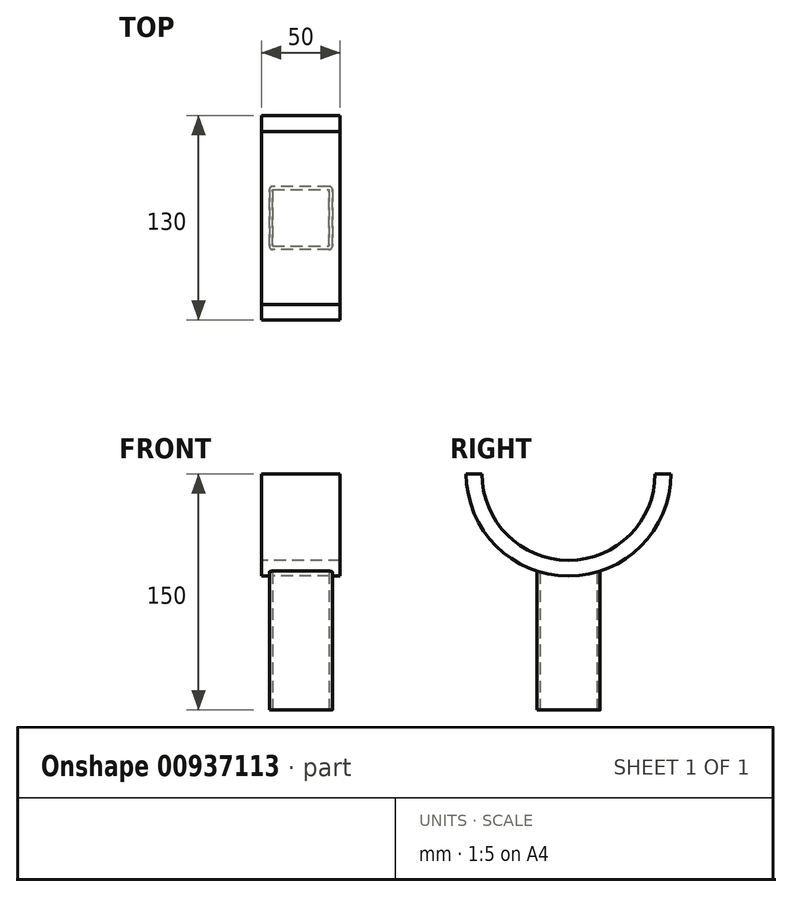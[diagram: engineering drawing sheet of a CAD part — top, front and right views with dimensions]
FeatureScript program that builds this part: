
annotation { "Feature Type Name" : "Feature", "Feature Type Description" : "" }
export const myFeature = defineFeature(function(context is Context, id is Id, definition is map)
    precondition{}
    {
        {
            var Q0;
            Q0=qCreatedBy(makeId("Right.planeOp"),FACE);
            var sketch = newSketch(context, id + "F0", { "sketchPlane" : qUnion([Q0])});
            skArc(sketch, "E0", {"start": v(55, 0) * mm, "mid": v(0, -55) * mm, "end": v(-55, 0) * mm});
            skArc(sketch, "E1.0", {"start": v(65, 0) * mm, "mid": v(0, -65) * mm, "end": v(-65, 0) * mm});
            skLineSegment(sketch, "E2", {"start": v(-65, 0) * mm, "end": v(-55, 0) * mm});
            skLineSegment(sketch, "E3", {"start": v(55, 0) * mm, "end": v(65, 0) * mm});
            skSolve(sketch);
        }
        {
            var Q0;
            Q0 = qSketchRegion(id + "F0", true);
            extrude(context, id + "F1", {"entities" : qUnion([Q0]), "endBound" : BoundingType.SYMMETRIC, "depth" : 50 * mm, "offsetDistance" : 25 * mm});
        }
        {
            var Q0;
            Q0=qCreatedBy(makeId("Top.planeOp"),FACE);
            cPlane(context, id + "F2", {"entities" : qUnion([Q0]), "cplaneType" : CPlaneType.OFFSET, "offset" : 150 * mm, "oppositeDirection" : true, "width" : 150 * mm, "height" : 150 * mm});
        }
        {
            var Q0;
            Q0=qCreatedBy(id+"F2.planeOp",FACE);
            var sketch = newSketch(context, id + "F3", { "sketchPlane" : qUnion([Q0])});
            skLineSegment(sketch, "E4.bottom", {"start": v(-18, 20) * mm, "end": v(18, 20) * mm});
            skLineSegment(sketch, "E4.top", {"start": v(-18, -20) * mm, "end": v(18, -20) * mm});
            skLineSegment(sketch, "E4.left", {"start": v(-20, 18) * mm, "end": v(-20, -18) * mm});
            skLineSegment(sketch, "E4.right", {"start": v(20, 18) * mm, "end": v(20, -18) * mm});
            skPoint(sketch, "E4.middle", {"position": v(0, 0) * mm});
            skPoint(sketch, "E5.visualSharp", {"position": v(-20, 20) * mm});
            skArc(sketch, "E5.filletArc", {"start": v(-18, 20) * mm, "mid": v(-19.41, 19.41) * mm, "end": v(-20, 18) * mm});
            skPoint(sketch, "E6.visualSharp", {"position": v(20, 20) * mm});
            skArc(sketch, "E6.filletArc", {"start": v(20, 18) * mm, "mid": v(19.41, 19.41) * mm, "end": v(18, 20) * mm});
            skPoint(sketch, "E7.visualSharp", {"position": v(20, -20) * mm});
            skArc(sketch, "E7.filletArc", {"start": v(18, -20) * mm, "mid": v(19.41, -19.41) * mm, "end": v(20, -18) * mm});
            skPoint(sketch, "E8.visualSharp", {"position": v(-20, -20) * mm});
            skArc(sketch, "E8.filletArc", {"start": v(-20, -18) * mm, "mid": v(-19.41, -19.41) * mm, "end": v(-18, -20) * mm});
            skSolve(sketch);
        }
        {
            var Q0;
            Q0 = qSketchRegion(id + "F3", true);
            extrude(context, id + "F4", {"entities" : qUnion([Q0]), "operationType" : NewBodyOperationType.ADD, "endBound" : BoundingType.UP_TO_NEXT, "depth" : 25 * mm, "offsetDistance" : 25 * mm});
        }
        {
            var Q0;
            Q0=makeQuery(id+"F4.opExtrude","CAP_FACE",FACE,{"disambiguationData":[OSD([sQuery(id+"F3.wireOp",EDGE,"E4.bottom"),sQuery(id+"F3.wireOp",EDGE,"E4.top"),sQuery(id+"F3.wireOp",EDGE,"E4.left"),sQuery(id+"F3.wireOp",EDGE,"E4.right"),sQuery(id+"F3.wireOp",EDGE,"E5.filletArc"),sQuery(id+"F3.wireOp",EDGE,"E6.filletArc"),sQuery(id+"F3.wireOp",EDGE,"E7.filletArc"),sQuery(id+"F3.wireOp",EDGE,"E8.filletArc")])],"isStart":true});
            var sketch = newSketch(context, id + "F5", { "sketchPlane" : qUnion([Q0])});
            skLineSegment(sketch, "E9.0", {"start": v(18, -18) * mm, "end": v(18, -18) * mm});
            skLineSegment(sketch, "E9.1", {"start": v(-18, -18) * mm, "end": v(18, -18) * mm});
            skLineSegment(sketch, "E9.2", {"start": v(18, -18) * mm, "end": v(18, 18) * mm});
            skLineSegment(sketch, "E9.3", {"start": v(-18, -18) * mm, "end": v(-18, -18) * mm});
            skLineSegment(sketch, "E9.4", {"start": v(18, 18) * mm, "end": v(18, 18) * mm});
            skLineSegment(sketch, "E9.5", {"start": v(-18, 18) * mm, "end": v(18, 18) * mm});
            skLineSegment(sketch, "E9.6", {"start": v(-18, 18) * mm, "end": v(-18, 18) * mm});
            skLineSegment(sketch, "E9.7", {"start": v(-18, -18) * mm, "end": v(-18, 18) * mm});
            skSolve(sketch);
        }
        {
            var Q0;
            Q0=makeQuery(id+"F5.imprint","IMPRINT",FACE,{"disambiguationData":[TD([[makeQuery(id+"F5.imprint","IMPRINT",EDGE,{"derivedFrom":sQuery(id+"F5.wireOp",EDGE,"E9.1")}),1.0]])]});
            var Q1;
            Q1=makeQuery(id+"F1.opExtrude","SWEPT_FACE",FACE,{"disambiguationData":[OSD([sQuery(id+"F0.wireOp",EDGE,"E1.0")])]});
            extrude(context, id + "F6", {"entities" : qUnion([Q0]), "operationType" : NewBodyOperationType.REMOVE, "endBound" : BoundingType.UP_TO_SURFACE, "oppositeDirection" : true, "depth" : 25 * mm, "endBoundEntityFace" : qUnion([Q1]), "offsetDistance" : 25 * mm});
        }
    });
